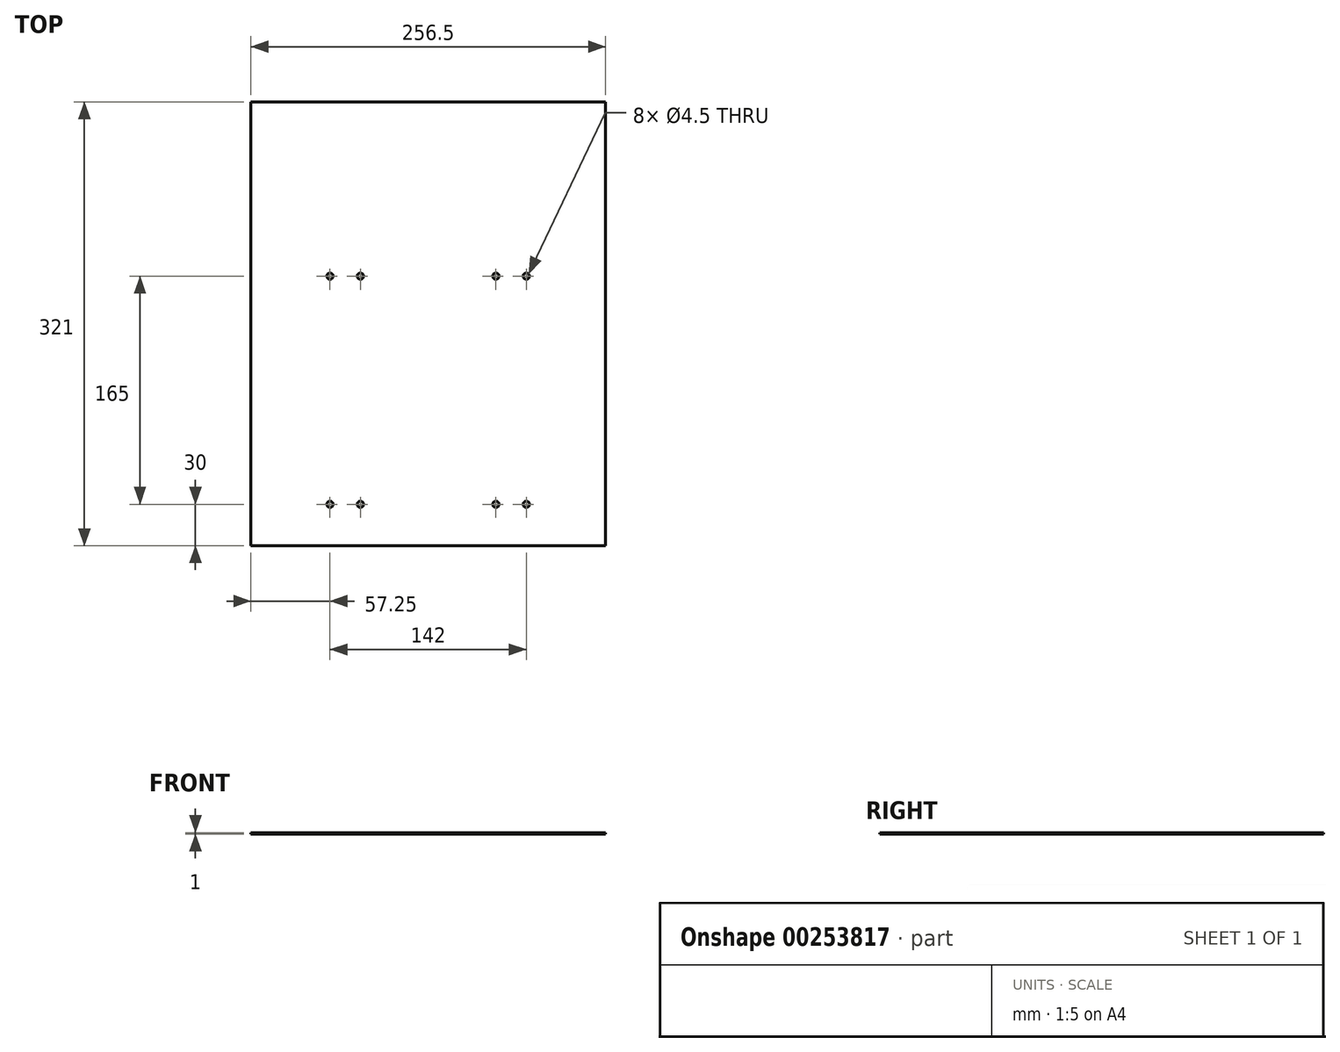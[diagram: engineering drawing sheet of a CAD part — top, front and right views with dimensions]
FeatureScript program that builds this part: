
annotation { "Feature Type Name" : "Feature", "Feature Type Description" : "" }
export const myFeature = defineFeature(function(context is Context, id is Id, definition is map)
    precondition{}
    {
        {
            var Q0;
            Q0=qCreatedBy(makeId("Top.planeOp"),FACE);
            var sketch = newSketch(context, id + "F0", { "sketchPlane" : qUnion([Q0])});
            skLineSegment(sketch, "E0.bottom", {"start": v(128.25, -160.5) * mm, "end": v(-128.25, -160.5) * mm});
            skLineSegment(sketch, "E0.top", {"start": v(128.25, 160.5) * mm, "end": v(-128.25, 160.5) * mm});
            skLineSegment(sketch, "E0.left", {"start": v(128.25, -160.5) * mm, "end": v(128.25, 160.5) * mm});
            skLineSegment(sketch, "E0.right", {"start": v(-128.25, -160.5) * mm, "end": v(-128.25, 160.5) * mm});
            skPoint(sketch, "E0.middle", {"position": v(0, 0) * mm});
            skSolve(sketch);
        }
        {
            var Q0;
            Q0 = qSketchRegion(id + "F0", true);
            extrude(context, id + "F1", {"entities" : qUnion([Q0]), "depth" : 1 * mm, "offsetDistance" : 25 * mm});
        }
        {
            var Q0;
            Q0=makeQuery(id+"F0.imprint","IMPRINT",FACE,{"disambiguationData":[TD([[makeQuery(id+"F0.imprint","IMPRINT",EDGE,{"derivedFrom":sQuery(id+"F0.wireOp",EDGE,"E0.bottom")}),-1.0]])]});
            var sketch = newSketch(context, id + "F2", { "sketchPlane" : qUnion([Q0])});
            skCircle(sketch, "E1", {"center": v(-71, 34.5) * mm, "radius": 2.25 * mm});
            skCircle(sketch, "E2", {"center": v(-49, 34.5) * mm, "radius": 2.25 * mm});
            skCircle(sketch, "E3", {"center": v(-71, -130.5) * mm, "radius": 2.25 * mm});
            skCircle(sketch, "E4", {"center": v(-49, -130.5) * mm, "radius": 2.25 * mm});
            skCircle(sketch, "E5.MirrorC", {"center": v(71, 34.5) * mm, "radius": 2.25 * mm});
            skCircle(sketch, "E6.MirrorC", {"center": v(49, 34.5) * mm, "radius": 2.25 * mm});
            skCircle(sketch, "E7.MirrorC", {"center": v(49, -130.5) * mm, "radius": 2.25 * mm});
            skCircle(sketch, "E8.MirrorC", {"center": v(71, -130.5) * mm, "radius": 2.25 * mm});
            skSolve(sketch);
        }
        {
            var Q0;
            Q0 = qSketchRegion(id + "F2", true);
            extrude(context, id + "F3", {"entities" : qUnion([Q0]), "operationType" : NewBodyOperationType.REMOVE, "endBound" : BoundingType.THROUGH_ALL, "depth" : 25 * mm, "offsetDistance" : 25 * mm});
        }
    });
